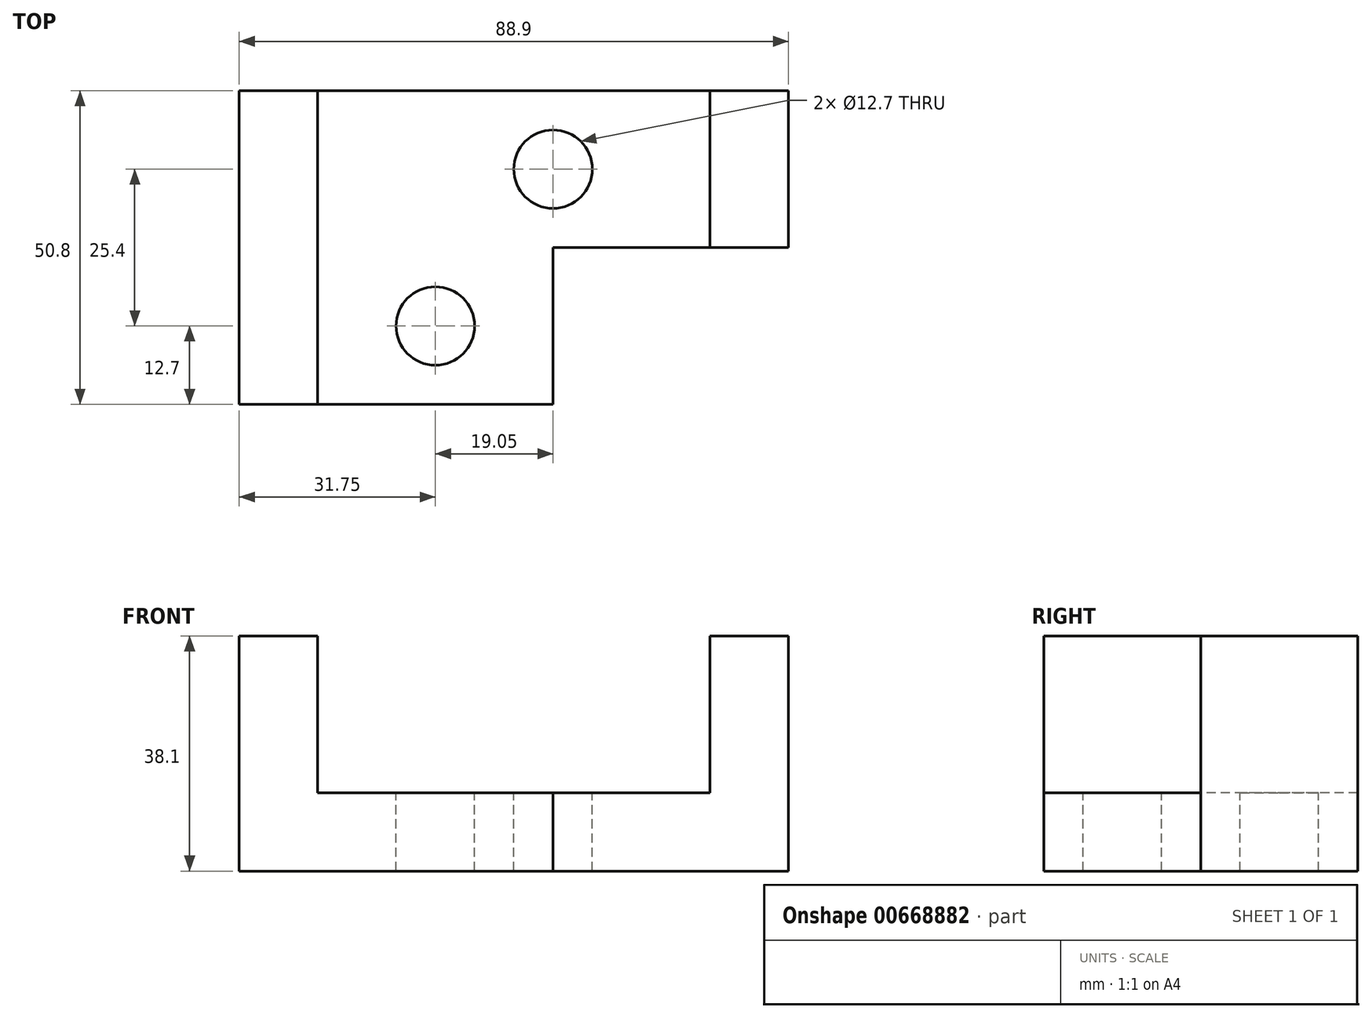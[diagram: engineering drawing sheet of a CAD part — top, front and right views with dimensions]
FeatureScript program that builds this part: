
annotation { "Feature Type Name" : "Feature", "Feature Type Description" : "" }
export const myFeature = defineFeature(function(context is Context, id is Id, definition is map)
    precondition{}
    {
        {
            var Q0;
            Q0=qCreatedBy(makeId("Front.planeOp"),FACE);
            var sketch = newSketch(context, id + "F0", { "sketchPlane" : qUnion([Q0])});
            skLineSegment(sketch, "E0.bottom", {"start": v(-44.45, 19.05) * mm, "end": v(44.45, 19.05) * mm});
            skLineSegment(sketch, "E0.top", {"start": v(-44.45, -19.05) * mm, "end": v(44.45, -19.05) * mm});
            skLineSegment(sketch, "E0.left", {"start": v(-44.45, 19.05) * mm, "end": v(-44.45, -19.05) * mm});
            skLineSegment(sketch, "E0.right", {"start": v(44.45, 19.05) * mm, "end": v(44.45, -19.05) * mm});
            skPoint(sketch, "E0.middle", {"position": v(0, 0) * mm});
            skSolve(sketch);
        }
        {
            var Q0;
            Q0=makeQuery(id+"F0.imprint","IMPRINT",FACE,{"disambiguationData":[TD([[makeQuery(id+"F0.imprint","IMPRINT",EDGE,{"derivedFrom":sQuery(id+"F0.wireOp",EDGE,"E0.bottom")}),-1.0]])]});
            extrude(context, id + "F1", {"entities" : qUnion([Q0]), "depth" : 50.8 * mm, "offsetDistance" : 25.4 * mm});
        }
        {
            var Q0;
            Q0=makeQuery(id+"F1.opExtrude","CAP_FACE",FACE,{"disambiguationData":[OSD([sQuery(id+"F0.wireOp",EDGE,"E0.bottom"),sQuery(id+"F0.wireOp",EDGE,"E0.top"),sQuery(id+"F0.wireOp",EDGE,"E0.left"),sQuery(id+"F0.wireOp",EDGE,"E0.right")])],"isStart":false});
            var sketch = newSketch(context, id + "F2", { "sketchPlane" : qUnion([Q0])});
            skLineSegment(sketch, "E1.bottom", {"start": v(-31.75, 19.05) * mm, "end": v(31.75, 19.05) * mm});
            skLineSegment(sketch, "E1.top", {"start": v(-31.75, -6.35) * mm, "end": v(31.75, -6.35) * mm});
            skLineSegment(sketch, "E1.left", {"start": v(-31.75, 19.05) * mm, "end": v(-31.75, -6.35) * mm});
            skLineSegment(sketch, "E1.right", {"start": v(31.75, 19.05) * mm, "end": v(31.75, -6.35) * mm});
            skSolve(sketch);
        }
        {
            var Q0;
            Q0=makeQuery(id+"F2.imprint","IMPRINT",FACE,{"disambiguationData":[TD([[makeQuery(id+"F2.imprint","IMPRINT",EDGE,{"derivedFrom":sQuery(id+"F2.wireOp",EDGE,"E1.bottom")}),-1.0]])]});
            extrude(context, id + "F3", {"entities" : qUnion([Q0]), "operationType" : NewBodyOperationType.REMOVE, "oppositeDirection" : true, "depth" : 50.8 * mm, "offsetDistance" : 25.4 * mm});
        }
        {
            var Q0;
            Q0=makeQuery(id+"F1.opExtrude","CAP_FACE",FACE,{"disambiguationData":[OSD([sQuery(id+"F0.wireOp",EDGE,"E0.bottom"),sQuery(id+"F0.wireOp",EDGE,"E0.top"),sQuery(id+"F0.wireOp",EDGE,"E0.left"),sQuery(id+"F0.wireOp",EDGE,"E0.right")])],"isStart":false});
            var sketch = newSketch(context, id + "F4", { "sketchPlane" : qUnion([Q0])});
            skLineSegment(sketch, "E2.bottom", {"start": v(44.45, -19.05) * mm, "end": v(6.35, -19.05) * mm});
            skLineSegment(sketch, "E2.top", {"start": v(44.45, -6.35) * mm, "end": v(6.35, -6.35) * mm});
            skLineSegment(sketch, "E2.left", {"start": v(44.45, -19.05) * mm, "end": v(44.45, -6.35) * mm});
            skLineSegment(sketch, "E2.right", {"start": v(6.35, -19.05) * mm, "end": v(6.35, -6.35) * mm});
            skLineSegment(sketch, "E3.bottom", {"start": v(31.75, 19.05) * mm, "end": v(44.45, 19.05) * mm});
            skLineSegment(sketch, "E3.top", {"start": v(31.75, -6.35) * mm, "end": v(44.45, -6.35) * mm});
            skLineSegment(sketch, "E3.left", {"start": v(31.75, 19.05) * mm, "end": v(31.75, -6.35) * mm});
            skLineSegment(sketch, "E3.right", {"start": v(44.45, 19.05) * mm, "end": v(44.45, -6.35) * mm});
            skSolve(sketch);
        }
        {
            var Q0;
            Q0=makeQuery(id+"F4.imprint","IMPRINT",FACE,{"disambiguationData":[TD([[makeQuery(id+"F4.imprint","IMPRINT",EDGE,{"derivedFrom":sQuery(id+"F4.wireOp",EDGE,"E2.bottom")}),1.0]])]});
            extrude(context, id + "F5", {"entities" : qUnion([Q0]), "operationType" : NewBodyOperationType.REMOVE, "oppositeDirection" : true, "depth" : 25.4 * mm, "offsetDistance" : 25.4 * mm});
        }
        {
            var Q0;
            {var subQ0=sQuery(id+"F0.wireOp",EDGE,"E0.bottom");var subQ1=sQuery(id+"F0.wireOp",EDGE,"E0.right");Q0=makeQuery(id+"F5.boolean.opBoolean","SPLIT",FACE,{"disambiguationData":[TD([makeQuery(id+"F1.opExtrude","SWEPT_FACE",FACE,{"disambiguationData":[OSD([subQ1])]})])],"derivedFrom":makeQuery(id+"F1.opExtrude","CAP_FACE",FACE,{"disambiguationData":[OSD([subQ0,sQuery(id+"F0.wireOp",EDGE,"E0.top"),sQuery(id+"F0.wireOp",EDGE,"E0.left"),subQ1])],"isStart":false})});}
            extrude(context, id + "F6", {"entities" : qUnion([Q0]), "operationType" : NewBodyOperationType.REMOVE, "oppositeDirection" : true, "depth" : 25.4 * mm, "offsetDistance" : 25.4 * mm});
        }
        {
            var Q0;
            Q0=makeQuery(id+"F3.boolean.opBoolean","COPY",FACE,{"derivedFrom":makeQuery(id+"F3.opExtrude","SWEPT_FACE",FACE,{"disambiguationData":[OSD([sQuery(id+"F2.wireOp",EDGE,"E1.top")])]})});
            var sketch = newSketch(context, id + "F7", { "sketchPlane" : qUnion([Q0])});
            skCircle(sketch, "E4", {"center": v(-12.7, -38.1) * mm, "radius": 6.35 * mm});
            skCircle(sketch, "E5", {"center": v(6.35, -12.7) * mm, "radius": 6.35 * mm});
            skSolve(sketch);
        }
        {
            var Q0;
            Q0=makeQuery(id+"F7.imprint","IMPRINT",FACE,{"disambiguationData":[TD([[makeQuery(id+"F7.imprint","IMPRINT",EDGE,{"derivedFrom":sQuery(id+"F7.wireOp",EDGE,"E5")}),1.0]])]});
            extrude(context, id + "F8", {"entities" : qUnion([Q0]), "operationType" : NewBodyOperationType.REMOVE, "oppositeDirection" : true, "depth" : 50.8 * mm, "offsetDistance" : 25.4 * mm});
        }
        {
            var Q0;
            Q0=makeQuery(id+"F7.imprint","IMPRINT",FACE,{"disambiguationData":[TD([[makeQuery(id+"F7.imprint","IMPRINT",EDGE,{"derivedFrom":sQuery(id+"F7.wireOp",EDGE,"E4")}),1.0]])]});
            extrude(context, id + "F9", {"entities" : qUnion([Q0]), "operationType" : NewBodyOperationType.REMOVE, "oppositeDirection" : true, "depth" : 50.8 * mm, "offsetDistance" : 25.4 * mm});
        }
    });
